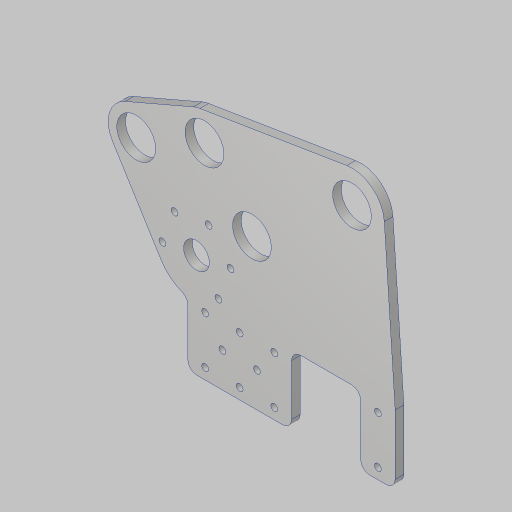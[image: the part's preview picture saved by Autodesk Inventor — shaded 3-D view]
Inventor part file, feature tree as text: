
AUTODESK INVENTOR PART (.ipt)
format: ipt  version: 2023.5 (Build 275446000, 446)  size: 269,824 bytes
history: native  units: in
note: dims shown in document units (in); Inventor stores cm internally (conversion verified against a paired STEP export)
features: sketch x3, extrude x3, hole x2, fillet x2, projected_geometry x1
ambient origin geometry x8: Origin, YZ Plane, XZ Plane, XY Plane, X Axis, Y Axis, Z Axis, Center Point
bodies: Solid1 (feature_tree)
feature tree (11):
  sketch  "Sketch1"  dims[d0=6.0in d1=2.0in]
  sketch  "Sketch2"  dims[d2=1.375in d3=0.5in d4=1.25in]
  extrude  "Extrusion1"  Depth=2.0in
  hole  "Hole1"  [1 undecoded]
  fillet  "Fillet1"  Radius=1.25in
  sketch  "Sketch4"  dims[d5=1.25in d6=1.375in d7=1.0in d8=0.375in d9=0.5in d10=0.5in d11=0.5in d12=0.5in d13=0.5in d14=4.38in d15=5.0in d16=3.0in d17=1.125in d18=0.375in d20=0.375in d21=0.375in d22=0.25in d23=0.0in d24=0.201in d25=0.75in d26=0.375in d27=0.25in d28=0.5635in d29=1.0in d30=0.8108in d31=6.5in d32=0.75in d33=0.26in d45=2.0in d46=2.4in d47=0.75in d48=0.5in d49=3.6in d50=0.25in d52=8.0in d53=2.0in d54=3.0in d55=1.125in d56=0.25in d57=1.0in d58=3.3in d59=2.275in d60=1.0in d61=3.3in d62=2.9288in d64=0.25in d65=0.25in d66=1.0in d67=0.0in d68=2.3622in d70=360.0deg d72=0.0in d73=0.0in d74=0.201in d75=0.75in d76=0.385in d77=0.25in d78=0.5635in d79=1.0in d80=0.8108in d82=3.342in d83=0.58in d85=0.26in d86=1.114in d92=6.3055in d93=5.834in d94=1.5551in]
  extrude  "Extrusion3"  Depth=0.26in
  extrude  "Extrusion4"  Depth=1.0in
  hole  "Hole2"  [1 undecoded]
  fillet  "Fillet4"  Radius=0.5in
  projected_geometry  "Project Cut Edges2"
note: 2 required parameter values undecoded (feature->parameter linkage not recoverable at this tier; creation-order binding heuristic only, values carry confidence <= 0.55)
